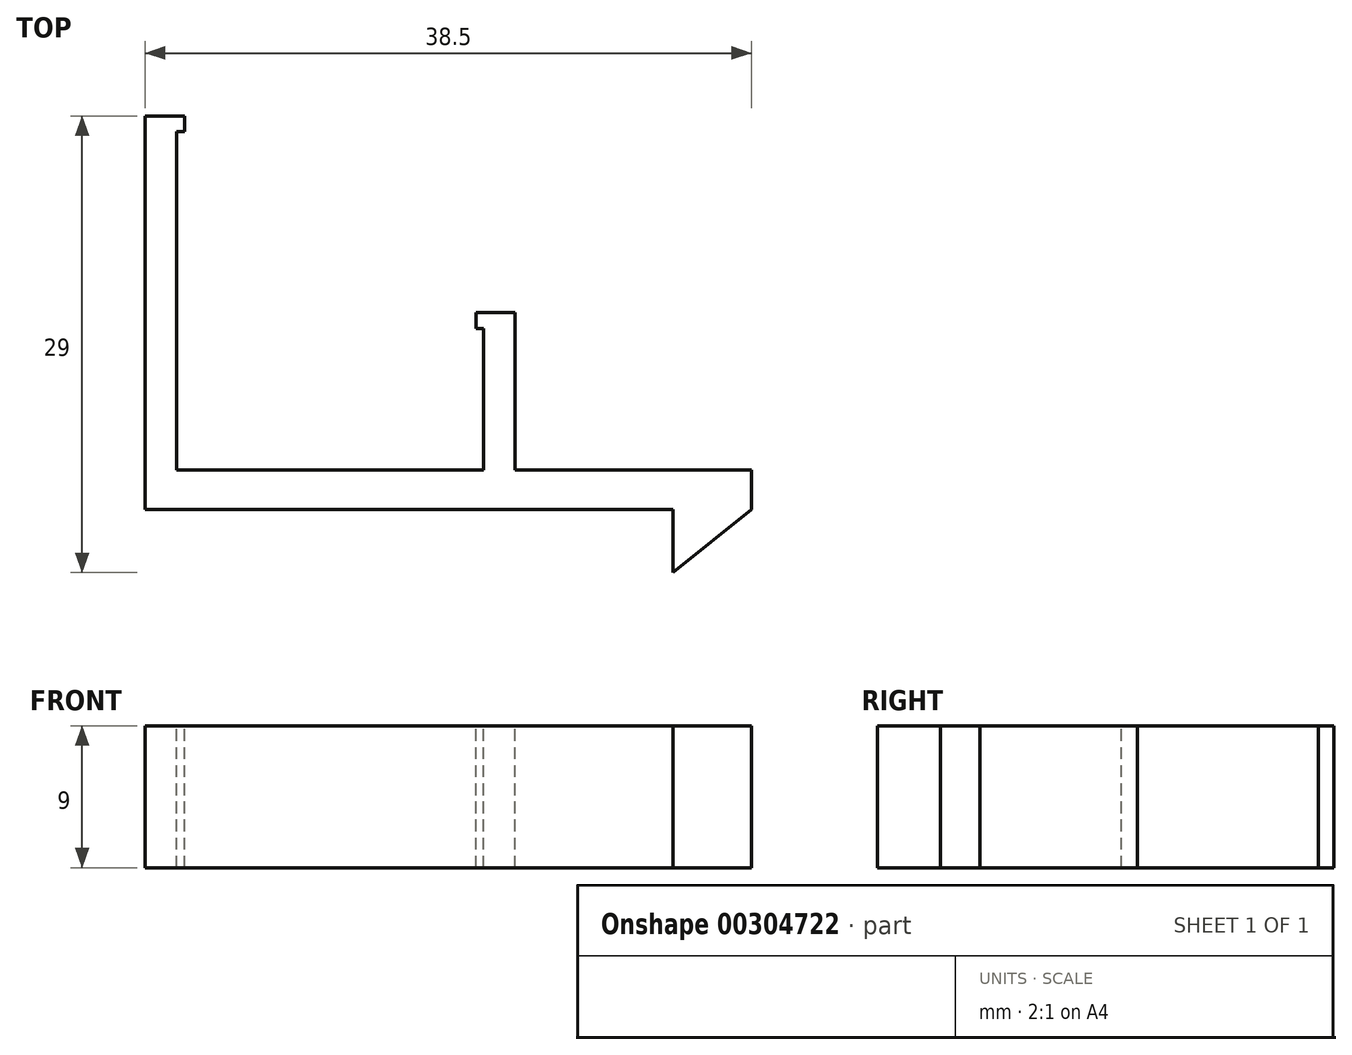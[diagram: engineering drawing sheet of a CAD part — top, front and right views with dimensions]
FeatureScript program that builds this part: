
annotation { "Feature Type Name" : "Feature", "Feature Type Description" : "" }
export const myFeature = defineFeature(function(context is Context, id is Id, definition is map)
    precondition{}
    {
        {
            var Q0;
            Q0=qCreatedBy(makeId("Top.planeOp"),FACE);
            var sketch = newSketch(context, id + "F0", { "sketchPlane" : qUnion([Q0])});
            skLineSegment(sketch, "E0", {"start": v(-21.5, -13.32) * mm, "end": v(-21.5, 11.68) * mm});
            skLineSegment(sketch, "E1", {"start": v(-21.5, 11.68) * mm, "end": v(-19.5, 11.68) * mm});
            skLineSegment(sketch, "E2", {"start": v(-19.5, 11.68) * mm, "end": v(-19.5, -10.82) * mm});
            skLineSegment(sketch, "E3", {"start": v(-19.5, -10.82) * mm, "end": v(0, -10.82) * mm});
            skLineSegment(sketch, "E4", {"start": v(0, -10.82) * mm, "end": v(0, -0.82) * mm});
            skLineSegment(sketch, "E5", {"start": v(0, -0.82) * mm, "end": v(2, -0.82) * mm});
            skLineSegment(sketch, "E6", {"start": v(2, -0.82) * mm, "end": v(2, -10.82) * mm});
            skLineSegment(sketch, "E7", {"start": v(2, -10.82) * mm, "end": v(17, -10.82) * mm});
            skLineSegment(sketch, "E8", {"start": v(17, -10.82) * mm, "end": v(17, -13.32) * mm});
            skLineSegment(sketch, "E9", {"start": v(17, -13.32) * mm, "end": v(-21.5, -13.32) * mm});
            skLineSegment(sketch, "E10", {"start": v(12.02, -13.32) * mm, "end": v(12.02, -17.32) * mm});
            skLineSegment(sketch, "E11", {"start": v(12.02, -17.32) * mm, "end": v(12.02, -17.32) * mm});
            skLineSegment(sketch, "E12", {"start": v(12.02, -17.32) * mm, "end": v(17, -13.32) * mm});
            skLineSegment(sketch, "E13.bottom", {"start": v(0, -0.82) * mm, "end": v(-0.5, -0.82) * mm});
            skLineSegment(sketch, "E13.top", {"start": v(0, -1.82) * mm, "end": v(-0.5, -1.82) * mm});
            skLineSegment(sketch, "E13.left", {"start": v(0, -0.82) * mm, "end": v(0, -1.82) * mm});
            skLineSegment(sketch, "E13.right", {"start": v(-0.5, -0.82) * mm, "end": v(-0.5, -1.82) * mm});
            skLineSegment(sketch, "E14.bottom", {"start": v(-19.5, 11.68) * mm, "end": v(-19, 11.68) * mm});
            skLineSegment(sketch, "E14.top", {"start": v(-19.5, 10.68) * mm, "end": v(-19, 10.68) * mm});
            skLineSegment(sketch, "E14.left", {"start": v(-19.5, 11.68) * mm, "end": v(-19.5, 10.68) * mm});
            skLineSegment(sketch, "E14.right", {"start": v(-19, 11.68) * mm, "end": v(-19, 10.68) * mm});
            skSolve(sketch);
        }
        {
            var Q0;
            {var subQ3=sQuery(id+"F0.wireOp",EDGE,"E0");Q0=makeQuery(id+"F0.imprint","IMPRINT",FACE,{"disambiguationData":[TD([[makeQuery(id+"F0.imprint","IMPRINT",EDGE,{"derivedFrom":subQ3}),-1.0]])]});}
            var Q1;
            Q1=makeQuery(id+"F0.imprint","IMPRINT",FACE,{"disambiguationData":[TD([[makeQuery(id+"F0.imprint","IMPRINT",EDGE,{"derivedFrom":sQuery(id+"F0.wireOp",EDGE,"E14.bottom")}),-1.0]])]});
            var Q2;
            Q2=makeQuery(id+"F0.imprint","IMPRINT",FACE,{"disambiguationData":[TD([[makeQuery(id+"F0.imprint","IMPRINT",EDGE,{"derivedFrom":sQuery(id+"F0.wireOp",EDGE,"E13.bottom")}),1.0]])]});
            var Q3;
            {var subQ2=sQuery(id+"F0.wireOp",EDGE,"E10");Q3=makeQuery(id+"F0.imprint","IMPRINT",FACE,{"disambiguationData":[TD([[makeQuery(id+"F0.imprint","IMPRINT",EDGE,{"derivedFrom":subQ2}),1.0]])]});}
            extrude(context, id + "F1", {"entities" : qUnion([Q0, Q1, Q2, Q3]), "oppositeDirection" : true, "depth" : 9 * mm});
        }
    });
